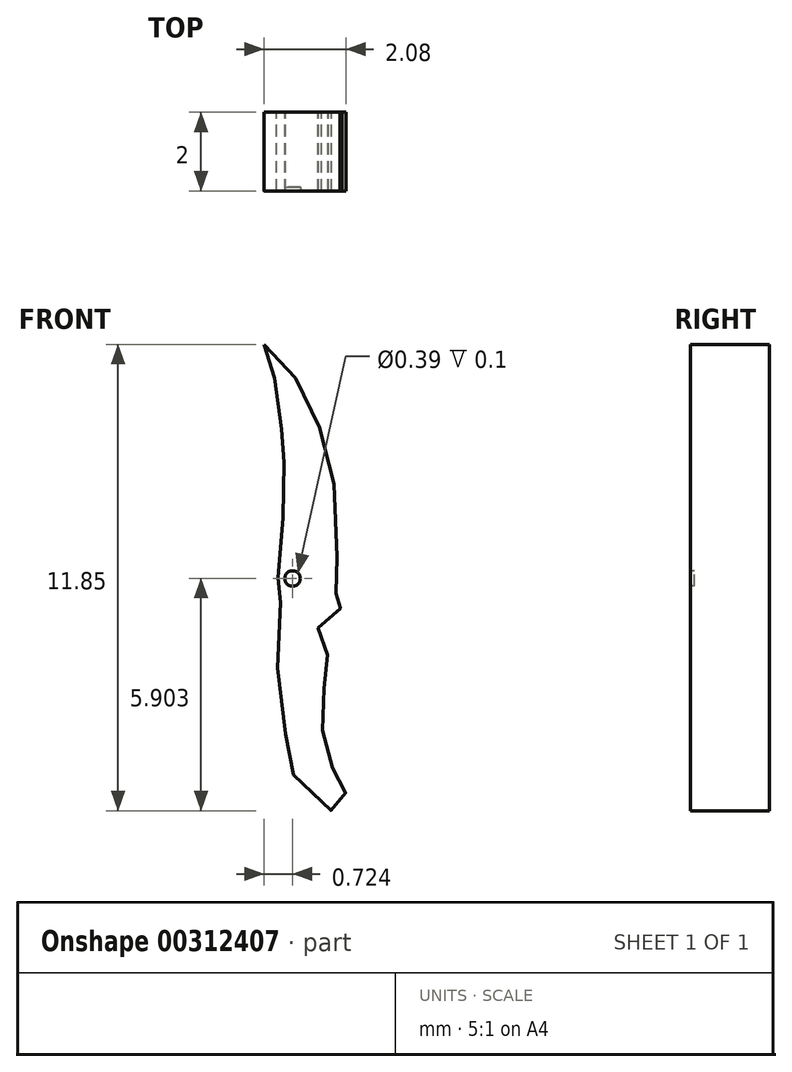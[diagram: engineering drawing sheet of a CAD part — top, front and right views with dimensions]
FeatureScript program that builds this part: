
annotation { "Feature Type Name" : "Feature", "Feature Type Description" : "" }
export const myFeature = defineFeature(function(context is Context, id is Id, definition is map)
    precondition{}
    {
        {
            var Q0;
            Q0=qCreatedBy(makeId("Front.planeOp"),FACE);
            var sketch = newSketch(context, id + "F0", { "sketchPlane" : qUnion([Q0])});
            skFitSpline(sketch, "E0", {"points": [v(-6.3, 14.59) * mm, v(-6.18, 14.36) * mm, v(-5.96, 13.28) * mm, v(-5.82, 12.16) * mm, v(-5.8, 11.73) * mm, v(-5.77, 10.55) * mm, v(-5.96, 8.7) * mm, v(-5.77, 8.27) * mm, v(-5.88, 8.04) * mm, v(-5.91, 5.76) * mm, v(-5.7, 4.27) * mm, v(-5.46, 3.5) * mm, v(-4.54, 2.75) * mm, v(-4.4, 3.01) * mm, v(-4.23, 3.19) * mm, v(-4.33, 3.5) * mm, v(-4.6, 3.9) * mm, v(-4.84, 4.61) * mm, v(-4.67, 5.63) * mm, v(-4.91, 6.15) * mm, v(-4.68, 6.79) * mm, v(-4.87, 7.11) * mm, v(-4.87, 7.52) * mm, v(-4.47, 7.8) * mm, v(-4.34, 8.02) * mm, v(-4.58, 8.24) * mm, v(-4.41, 8.28) * mm, v(-4.42, 8.71) * mm, v(-4.52, 11.04) * mm, v(-4.94, 12.6) * mm, v(-5.66, 13.95) * mm, v(-6.3, 14.59) * mm]});
            skSolve(sketch);
        }
        {
            var Q0;
            Q0 = qSketchRegion(id + "F0", true);
            extrude(context, id + "F1", {"entities" : qUnion([Q0]), "depth" : 2 * mm});
        }
        {
            var Q0;
            Q0=makeQuery(id+"F1.opExtrude","CAP_FACE",FACE,{"disambiguationData":[OSD([sQuery(id+"F0.wireOp",EDGE,"E0")])],"isStart":false});
            var sketch = newSketch(context, id + "F2", { "sketchPlane" : qUnion([Q0])});
            skCircle(sketch, "E1", {"center": v(-5.58, 8.64) * mm, "radius": 0.2 * mm});
            skSolve(sketch);
        }
        {
            var Q0;
            Q0 = qSketchRegion(id + "F2", true);
            extrude(context, id + "F3", {"entities" : qUnion([Q0]), "operationType" : NewBodyOperationType.REMOVE, "oppositeDirection" : true, "depth" : 0.1 * mm});
        }
    });
